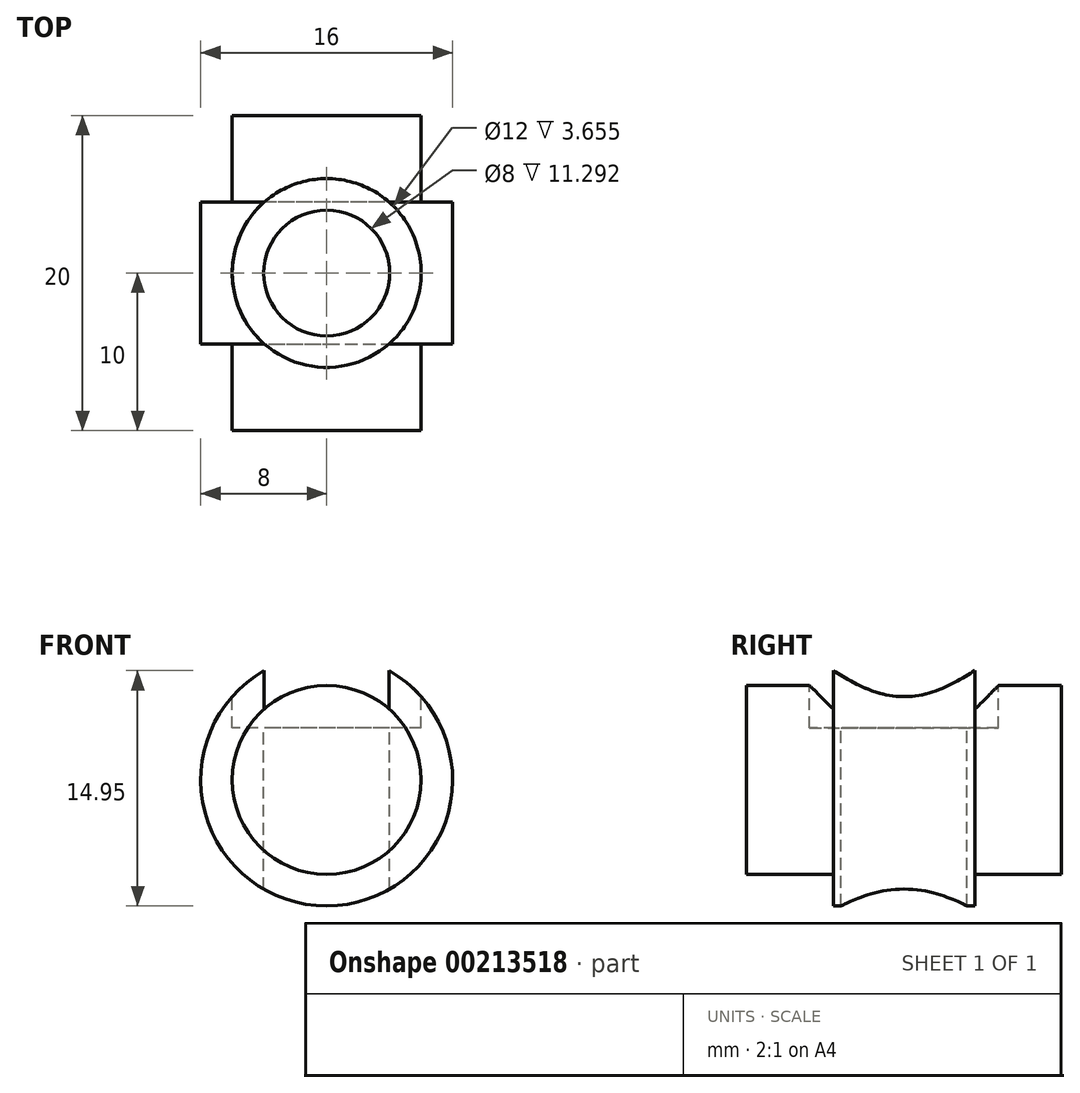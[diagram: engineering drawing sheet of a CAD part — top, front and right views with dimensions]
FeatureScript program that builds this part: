
annotation { "Feature Type Name" : "Feature", "Feature Type Description" : "" }
export const myFeature = defineFeature(function(context is Context, id is Id, definition is map)
    precondition{}
    {
        {
            var Q0;
            Q0=qCreatedBy(makeId("Front.planeOp"),FACE);
            var sketch = newSketch(context, id + "F0", { "sketchPlane" : qUnion([Q0])});
            skCircle(sketch, "E0", {"center": v(0, 0) * mm, "radius": 8 * mm});
            skSolve(sketch);
        }
        {
            var Q0;
            Q0 = qSketchRegion(id + "F0", true);
            extrude(context, id + "F1", {"entities" : qUnion([Q0]), "depth" : 20 * mm});
        }
        {
            var Q0;
            Q0=qCreatedBy(makeId("Top.planeOp"),FACE);
            cPlane(context, id + "F2", {"entities" : qUnion([Q0]), "cplaneType" : CPlaneType.OFFSET, "offset" : 8 * mm, "width" : 150 * mm, "height" : 150 * mm});
        }
        {
            var Q0;
            Q0=qCreatedBy(id+"F2.planeOp",FACE);
            var sketch = newSketch(context, id + "F3", { "sketchPlane" : qUnion([Q0])});
            skPoint(sketch, "E1", {"position": v(0, -10) * mm});
            skSolve(sketch);
        }
        {
            var Q0;
            Q0=sQuery(id+"F3.wireOp",VERTEX,"E1");
            var Q1;
            Q1=makeQuery(id+"F1.opExtrude","SWEPT_BODY",BODY,{"disambiguationData":[OSD([sQuery(id+"F0.wireOp",EDGE,"E0")])]});
            hole(context, id + "F4", {"style" : HoleStyle.C_BORE, "endStyle" : HoleEndStyle.THROUGH, "holeDiameter" : 8 * mm, "cBoreDiameter" : 12 * mm, "cBoreDepth" : 2 * mm, "locations" : qUnion([Q0]), "scope" : qUnion([Q1]), "isTappedThrough" : true});
        }
        {
            var Q0;
            Q0=makeQuery(id+"F1.opExtrude","CAP_FACE",FACE,{"disambiguationData":[OSD([sQuery(id+"F0.wireOp",EDGE,"E0")])],"isStart":true});
            var sketch = newSketch(context, id + "F5", { "sketchPlane" : qUnion([Q0])});
            skCircle(sketch, "E2", {"center": v(0, 0) * mm, "radius": 9 * mm});
            skCircle(sketch, "E3", {"center": v(0, 0) * mm, "radius": 6 * mm});
            skSolve(sketch);
        }
        {
            var Q0;
            Q0 = qSketchRegion(id + "F5", true);
            extrude(context, id + "F6", {"entities" : qUnion([Q0]), "operationType" : NewBodyOperationType.REMOVE, "oppositeDirection" : true, "depth" : 5.5 * mm});
        }
        {
            var Q0;
            Q0=makeQuery(id+"F1.opExtrude","CAP_FACE",FACE,{"disambiguationData":[OSD([sQuery(id+"F0.wireOp",EDGE,"E0")])],"isStart":false});
            var sketch = newSketch(context, id + "F7", { "sketchPlane" : qUnion([Q0])});
            skCircle(sketch, "E4", {"center": v(0, 0) * mm, "radius": 9 * mm});
            skCircle(sketch, "E5", {"center": v(0, 0) * mm, "radius": 6 * mm});
            skSolve(sketch);
        }
        {
            var Q0;
            Q0 = qSketchRegion(id + "F7", true);
            extrude(context, id + "F8", {"entities" : qUnion([Q0]), "operationType" : NewBodyOperationType.REMOVE, "oppositeDirection" : true, "depth" : 5.5 * mm});
        }
    });
